FCSTD DOCUMENT  (FreeCAD 1.0R39109 (Git))
Label: asm_cam_mount
License: All rights reserved
LicenseURL: https://en.wikipedia.org/wiki/All_rights_reserved
objects: App::Link×10, App::FeaturePython×10, Assembly::JointGroup×1, Assembly::AssemblyObject×1
EXTERNAL_REF file=../parts/cam_holder/cam_holder_base.FCStd obj=Body
EXTERNAL_REF file=../downloads/raspberry_pi_camera.FCStd obj=Raspberry_Pi_HQ_Camera_with_cs_mount_lens_v3
EXTERNAL_REF file=../secondary/bolts.FCStd obj=Body003
EXTERNAL_REF file=../secondary/bolts.FCStd obj=Body002

FEATURE [App::Link] cam_holder_base
  LinkPlacement = pos=(0,0,0) rot=(1,0,0;3.14159rad)
  LinkedObject = -> <external ../parts/cam_holder/cam_holder_base.FCStd>#Body
  Placement = pos=(0,0,0) rot=(1,0,0;3.14159rad)
FEATURE [App::FeaturePython] GroundedJoint  # Assembly grounded joint (typed FeaturePython)
  ObjectToGround = -> cam_holder_base
  Placement = pos=(0,0,0) rot=(1,0,0;3.14159rad)
FEATURE [App::Link] Raspberry_Pi_HQ_Camera_with_cs_mount_lens_v014  label="Raspberry Pi HQ Camera with cs mount lens v014"
  LinkPlacement = pos=(-18.96,19,-3.8) rot=(1,0,0;1.5708rad)
  LinkedObject = -> <external ../downloads/raspberry_pi_camera.FCStd>#Raspberry_Pi_HQ_Camera_with_cs_mount_lens_v3
  Placement = pos=(-18.96,19,-3.8) rot=(1,0,0;1.5708rad)
FEATURE [App::FeaturePython] Joint  label="Fixed"  # Assembly joint (typed FeaturePython)
  Activated = true
  AngleMax = 0
  AngleMin = 0
  Detach1 = false
  Detach2 = false
  Distance = 0
  Distance2 = 0
  EnableAngleMax = false
  EnableAngleMin = false
  EnableLengthMax = false
  EnableLengthMin = false
  JointType = 0 (Fixed)
  LengthMax = 0
  LengthMin = 0
  Placement1 = pos=(-14.96,-15,2.5) rot=(0,0,1;0rad)
  Placement2 = pos=(4,1.3,4) rot=(-1,0,0;1.5708rad)
  Reference1 = -> Assembly [cam_holder_base.Edge44,cam_holder_base.Edge44]
  Reference2 = -> Assembly [Raspberry_Pi_HQ_Camera_with_cs_mount_lens_v014.Part__Feature.Edge16,Raspberry_Pi_HQ_Camera_with_cs_mount_lens_v014.Part__Feature.Edge16]
FEATURE [App::Link] Hex_screw_M2_5_04_0  label="Hex screw M2.5 04.0"
  LinkPlacement = pos=(-7.97317,-20.5575,-6.3) rot=(0,0,1;0rad)
  LinkedObject = -> <external ../secondary/bolts.FCStd>#Body003
  Placement = pos=(-7.97317,-20.5575,-6.3) rot=(0,0,1;0rad)
FEATURE [App::Link] Hex_screw_M2_5_04_001  label="Hex screw M2.5 04.001"
  LinkPlacement = pos=(22.0268,-20.5575,-6.3) rot=(0,0,1;0rad)
  LinkedObject = -> <external ../secondary/bolts.FCStd>#Body003
  Placement = pos=(22.0268,-20.5575,-6.3) rot=(0,0,1;0rad)
FEATURE [App::Link] Hex_screw_M2_5_04_002  label="Hex screw M2.5 04.002"
  LinkPlacement = pos=(22.0268,-50.5575,-6.3) rot=(0,0,1;0rad)
  LinkedObject = -> <external ../secondary/bolts.FCStd>#Body003
  Placement = pos=(22.0268,-50.5575,-6.3) rot=(0,0,1;0rad)
FEATURE [App::Link] Hex_screw_M2_5_04_003  label="Hex screw M2.5 04.003"
  LinkPlacement = pos=(-7.97317,-50.5575,-6.3) rot=(0,0,1;0rad)
  LinkedObject = -> <external ../secondary/bolts.FCStd>#Body003
  Placement = pos=(-7.97317,-50.5575,-6.3) rot=(0,0,1;0rad)
FEATURE [App::FeaturePython] Joint001  label="Fixed001"  # Assembly joint (typed FeaturePython)
  Activated = true
  AngleMax = 0
  AngleMin = 0
  Detach1 = false
  Detach2 = false
  Distance = 0
  Distance2 = 0
  EnableAngleMax = false
  EnableAngleMin = false
  EnableLengthMax = false
  EnableLengthMin = false
  JointType = 0 (Fixed)
  LengthMax = 0
  LengthMin = 0
  Placement1 = pos=(-6.98683,35.5575,2.5) rot=(0,0,1;0rad)
  Placement2 = pos=(4,0,4) rot=(1,0,0;1.5708rad)
  Reference1 = -> Assembly [Hex_screw_M2_5_04_0.Edge4,Hex_screw_M2_5_04_0.Edge4]
  Reference2 = -> Assembly [Raspberry_Pi_HQ_Camera_with_cs_mount_lens_v014.Part__Feature.Edge18,Raspberry_Pi_HQ_Camera_with_cs_mount_lens_v014.Part__Feature.Edge18]
FEATURE [App::FeaturePython] Joint002  label="Fixed002"  # Assembly joint (typed FeaturePython)
  Activated = true
  AngleMax = 0
  AngleMin = 0
  Detach1 = false
  Detach2 = false
  Distance = 0
  Distance2 = 0
  EnableAngleMax = false
  EnableAngleMin = false
  EnableLengthMax = false
  EnableLengthMin = false
  JointType = 0 (Fixed)
  LengthMax = 0
  LengthMin = 0
  Placement1 = pos=(-6.98683,35.5575,2.5) rot=(0,0,1;0rad)
  Placement2 = pos=(34,0,4) rot=(1,0,0;1.5708rad)
  Reference1 = -> Assembly [Hex_screw_M2_5_04_001.Edge4,Hex_screw_M2_5_04_001.Edge4]
  Reference2 = -> Assembly [Raspberry_Pi_HQ_Camera_with_cs_mount_lens_v014.Part__Feature.Edge24,Raspberry_Pi_HQ_Camera_with_cs_mount_lens_v014.Part__Feature.Edge24]
FEATURE [App::FeaturePython] Joint003  label="Fixed003"  # Assembly joint (typed FeaturePython)
  Activated = true
  AngleMax = 0
  AngleMin = 0
  Detach1 = false
  Detach2 = false
  Distance = 0
  Distance2 = 0
  EnableAngleMax = false
  EnableAngleMin = false
  EnableLengthMax = false
  EnableLengthMin = false
  JointType = 0 (Fixed)
  LengthMax = 0
  LengthMin = 0
  Placement1 = pos=(-6.98683,35.5575,2.5) rot=(0,0,1;0rad)
  Placement2 = pos=(34,0,34) rot=(1,0,0;1.5708rad)
  Reference1 = -> Assembly [Hex_screw_M2_5_04_002.Edge4,Hex_screw_M2_5_04_002.Edge4]
  Reference2 = -> Assembly [Raspberry_Pi_HQ_Camera_with_cs_mount_lens_v014.Part__Feature.Edge22,Raspberry_Pi_HQ_Camera_with_cs_mount_lens_v014.Part__Feature.Edge22]
FEATURE [App::FeaturePython] Joint004  label="Fixed004"  # Assembly joint (typed FeaturePython)
  Activated = true
  AngleMax = 0
  AngleMin = 0
  Detach1 = false
  Detach2 = false
  Distance = 0
  Distance2 = 0
  EnableAngleMax = false
  EnableAngleMin = false
  EnableLengthMax = false
  EnableLengthMin = false
  JointType = 0 (Fixed)
  LengthMax = 0
  LengthMin = 0
  Placement1 = pos=(-6.98683,35.5575,2.5) rot=(0,0,1;0rad)
  Placement2 = pos=(4,0,34) rot=(1,0,0;1.5708rad)
  Reference1 = -> Assembly [Hex_screw_M2_5_04_003.Edge4,Hex_screw_M2_5_04_003.Edge4]
  Reference2 = -> Assembly [Raspberry_Pi_HQ_Camera_with_cs_mount_lens_v014.Part__Feature.Edge20,Raspberry_Pi_HQ_Camera_with_cs_mount_lens_v014.Part__Feature.Edge20]
FEATURE [App::Link] Hex_screw_M4_10_0  label="Hex screw M4 10.0"
  LinkPlacement = pos=(-25.9732,-58.0575,-20.5) rot=(0,0,1;0rad)
  LinkedObject = -> <external ../secondary/bolts.FCStd>#Body002
  Placement = pos=(-25.9732,-58.0575,-20.5) rot=(0,0,1;0rad)
FEATURE [App::Link] Hex_screw_M4_10_001  label="Hex screw M4 10.001"
  LinkPlacement = pos=(-25.9732,-20.0575,-20.5) rot=(0,0,1;0rad)
  LinkedObject = -> <external ../secondary/bolts.FCStd>#Body002
  Placement = pos=(-25.9732,-20.0575,-20.5) rot=(0,0,1;0rad)
FEATURE [App::Link] Hex_screw_M4_10_002  label="Hex screw M4 10.002"
  LinkPlacement = pos=(39.9468,-58.0575,-20.5) rot=(0,0,1;0rad)
  LinkedObject = -> <external ../secondary/bolts.FCStd>#Body002
  Placement = pos=(39.9468,-58.0575,-20.5) rot=(0,0,1;0rad)
FEATURE [App::Link] Hex_screw_M4_10_003  label="Hex screw M4 10.003"
  LinkPlacement = pos=(39.9468,-20.0575,-20.5) rot=(0,0,1;0rad)
  LinkedObject = -> <external ../secondary/bolts.FCStd>#Body002
  Placement = pos=(39.9468,-20.0575,-20.5) rot=(0,0,1;0rad)
FEATURE [App::FeaturePython] Joint005  label="Fixed005"  # Assembly joint (typed FeaturePython)
  Activated = true
  AngleMax = 0
  AngleMin = 0
  Detach1 = false
  Detach2 = false
  Distance = 0
  Distance2 = 0
  EnableAngleMax = false
  EnableAngleMin = false
  EnableLengthMax = false
  EnableLengthMin = false
  JointType = 0 (Fixed)
  LengthMax = 0
  LengthMin = 0
  Placement1 = pos=(-6.98683,35.5575,10) rot=(0,0,1;0rad)
  Placement2 = pos=(32.96,-15.5,10.5) rot=(0,0,1;0rad)
  Reference1 = -> Assembly [Hex_screw_M4_10_003.Edge3,Hex_screw_M4_10_003.Edge3]
  Reference2 = -> Assembly [cam_holder_base.Edge93,cam_holder_base.Edge93]
FEATURE [App::FeaturePython] Joint006  label="Fixed006"  # Assembly joint (typed FeaturePython)
  Activated = true
  AngleMax = 0
  AngleMin = 0
  Detach1 = false
  Detach2 = false
  Distance = 0
  Distance2 = 0
  EnableAngleMax = false
  EnableAngleMin = false
  EnableLengthMax = false
  EnableLengthMin = false
  JointType = 0 (Fixed)
  LengthMax = 0
  LengthMin = 0
  Placement1 = pos=(-6.98683,35.5575,10) rot=(0,0,1;0rad)
  Placement2 = pos=(32.96,22.5,10.5) rot=(0,0,1;0rad)
  Reference1 = -> Assembly [Hex_screw_M4_10_002.Edge3,Hex_screw_M4_10_002.Edge3]
  Reference2 = -> Assembly [cam_holder_base.Edge89,cam_holder_base.Edge89]
FEATURE [App::FeaturePython] Joint007  label="Fixed007"  # Assembly joint (typed FeaturePython)
  Activated = true
  AngleMax = 0
  AngleMin = 0
  Detach1 = false
  Detach2 = false
  Distance = 0
  Distance2 = 0
  EnableAngleMax = false
  EnableAngleMin = false
  EnableLengthMax = false
  EnableLengthMin = false
  JointType = 0 (Fixed)
  LengthMax = 0
  LengthMin = 0
  Placement1 = pos=(-6.98683,35.5575,10) rot=(0,0,1;0rad)
  Placement2 = pos=(-32.96,-15.5,10.5) rot=(0,0,1;0rad)
  Reference1 = -> Assembly [Hex_screw_M4_10_001.Edge3,Hex_screw_M4_10_001.Edge3]
  Reference2 = -> Assembly [cam_holder_base.Edge74,cam_holder_base.Edge74]
FEATURE [App::FeaturePython] Joint008  label="Fixed008"  # Assembly joint (typed FeaturePython)
  Activated = true
  AngleMax = 0
  AngleMin = 0
  Detach1 = false
  Detach2 = false
  Distance = 0
  Distance2 = 0
  EnableAngleMax = false
  EnableAngleMin = false
  EnableLengthMax = false
  EnableLengthMin = false
  JointType = 0 (Fixed)
  LengthMax = 0
  LengthMin = 0
  Placement1 = pos=(-6.98683,35.5575,10) rot=(0,0,1;0rad)
  Placement2 = pos=(-32.96,22.5,10.5) rot=(0,0,1;0rad)
  Reference1 = -> Assembly [Hex_screw_M4_10_0.Edge3,Hex_screw_M4_10_0.Edge3]
  Reference2 = -> Assembly [cam_holder_base.Edge85,cam_holder_base.Edge85]
FEATURE [Assembly::JointGroup] Joints
  Group = -> [GroundedJoint,Joint,Joint001,Joint002,Joint003,Joint004,Joint005,Joint006,Joint007,Joint008]
FEATURE [Assembly::AssemblyObject] Assembly  label="asm_cam_mount"
  Group = -> [Joints,cam_holder_base,GroundedJoint,Raspberry_Pi_HQ_Camera_with_cs_mount_lens_v014,Joint,Hex_screw_M2_5_04_0,Hex_screw_M2_5_04_001,Hex_screw_M2_5_04_002,Hex_screw_M2_5_04_003,Joint001,Joint002,Joint003,Joint004,Hex_screw_M4_10_0,Hex_screw_M4_10_001,Hex_screw_M4_10_002,Hex_screw_M4_10_003,Joint005,Joint006,Joint007,Joint008]
  Origin = -> Origin
  Type = Assembly

RESOLVED EXTERNAL PARTS (link-assembly join: the EXTERNAL_REF files above that resolve inside this repo's crawl, each included once):
---- part ../parts/cam_holder/cam_holder_base.FCStd = doc fcstd_f22dad3d8907 ----
FCSTD DOCUMENT  (FreeCAD 1.0R39109 (Git))
Label: cam_holder_base
License: All rights reserved
LicenseURL: https://en.wikipedia.org/wiki/All_rights_reserved
objects: Sketcher::SketchObject×4, PartDesign::Pad×3, PartDesign::Body×1
note: 18 computed .brp shape members not serialized (recipe doc carries the construction recipe); baked Part::Feature solids carry a one-line shape summary decoded from their .brp

FEATURE [Sketcher::SketchObject] Sketch
  ArcFitTolerance = 0
  FullyConstrained = true
  MakeInternals = false
  sketch-geometry (27):
    g0: LineSegment [constr] StartX=-19.96 StartY=19 StartZ=0 EndX=-19.96 EndY=-14 EndZ=0
    g1: LineSegment StartX=-19.96 StartY=-19 StartZ=0 EndX=-11.96 EndY=-19 EndZ=0
    g2: LineSegment [constr] StartX=20 StartY=-14 StartZ=0 EndX=20 EndY=19 EndZ=0
    g3: LineSegment [constr] StartX=20 StartY=19 StartZ=0 EndX=-19.96 EndY=19 EndZ=0
    g4: GeomPoint [constr] X=0 Y=0 Z=0
    g5: Circle CenterX=-14.96 CenterY=15 CenterZ=0 NormalX=0 NormalY=0 NormalZ=1 AngleXU=0 Radius=1.725
    g6: Circle CenterX=15 CenterY=15 CenterZ=0 NormalX=0 NormalY=0 NormalZ=1 AngleXU=0 Radius=1.725
    g7: Circle CenterX=-14.96 CenterY=-15 CenterZ=0 NormalX=0 NormalY=0 NormalZ=1 AngleXU=0 Radius=1.725
    g8: Circle CenterX=15 CenterY=-15 CenterZ=0 NormalX=0 NormalY=0 NormalZ=1 AngleXU=0 Radius=1.725
    g9: ArcOfCircle CenterX=0 CenterY=0 CenterZ=0 NormalX=0 NormalY=0 NormalZ=1 AngleXU=0 Radius=18.05 StartAngle=5.41371 EndAngle=7.54435
    g10: LineSegment StartX=-11.96 StartY=-19 StartZ=0 EndX=-11.96 EndY=-15 EndZ=0
    g11: LineSegment StartX=11.96 StartY=-19 StartZ=0 EndX=11.96 EndY=-15 EndZ=0
    g12: LineSegment StartX=11.96 StartY=-19 StartZ=0 EndX=20.04 EndY=-19 EndZ=0
    g13: LineSegment StartX=-5.5 StartY=21.5 StartZ=0 EndX=5.5 EndY=21.5 EndZ=0
    g14: LineSegment StartX=-5.5 StartY=21.5 StartZ=0 EndX=-5.5 EndY=17.1916 EndZ=0
    g15: LineSegment StartX=5.5 StartY=21.5 StartZ=0 EndX=5.5 EndY=17.1916 EndZ=0
    g16: ArcOfCircle CenterX=0 CenterY=0 CenterZ=0 NormalX=0 NormalY=0 NormalZ=1 AngleXU=0 Radius=18.05 StartAngle=1.88043 EndAngle=4.01106
    g17: LineSegment StartX=-20 StartY=26 StartZ=0 EndX=20 EndY=26 EndZ=0
    g18: LineSegment StartX=-11.96 StartY=-15 StartZ=0 EndX=-11.6464 EndY=-13.79 EndZ=0
    g19: LineSegment StartX=11.96 StartY=-15 StartZ=0 EndX=11.6464 EndY=-13.79 EndZ=0
    g20: GeomPoint [constr] X=-19.96 Y=-14 Z=0
    g21: LineSegment StartX=-25.96 StartY=26 StartZ=0 EndX=-25.96 EndY=-19 EndZ=0
    g22: LineSegment StartX=-19.96 StartY=-19 StartZ=0 EndX=-25.96 EndY=-19 EndZ=0
    g23: LineSegment StartX=-20 StartY=26 StartZ=0 EndX=-25.96 EndY=26 EndZ=0
    g24: LineSegment StartX=20.04 StartY=-19 StartZ=0 EndX=25.96 EndY=-19 EndZ=0
    g25: LineSegment StartX=25.96 StartY=-19 StartZ=0 EndX=25.96 EndY=26 EndZ=0
    g26: LineSegment StartX=25.96 StartY=26 StartZ=0 EndX=20 EndY=26 EndZ=0
  constraints (77):
    c: Coincident(g2,g3)
    c: Coincident(g3,g0)
    c: Horizontal(g1)
    c: Horizontal(g3)
    c: Vertical(g0)
    c: Vertical(g2)
    c: Coincident(g4,g-1)
    c: DistanceX(g1,g12) = 40
    c: DistanceY(g1,g0) = 38
    c: Distance(g5,g0) = 5
    c: Distance(g5,g3) = 4
    c: Equal(g5,g6)
    c: Equal(g5,g7)
    c: Equal(g5,g8)
    c: Diameter(g5) = 3.45
    c: Vertical(g6,g8)
    c: Horizontal(g7,g8)
    c: Horizontal(g5,g6)
    c: Vertical(g5,g7)
    c: Distance(g4,g2) = 20
    c: Distance(g6,g2) = 5
    c: Distance(g7,g1) = 4
    c: Distance(g4,g1) = 19
    c: Coincident(g9,g4)
    c: Diameter(g9) = 36.1
    c: Vertical(g10)
    c: Distance(g10) = 4
    c: DistanceX(g1,g10) = 8
    c: Symmetric(g11,g10,g-2)
    c: Parallel(g11,g10)
    c: Coincident(g1,g10)
    c: Coincident(g12,g11)
    c: Horizontal(g13)
    c: Distance(g13,g3) = 2.5
    c: Distance(g13,g-2) = 5.5
    c: DistanceX(g13,g13) = 11
    c: Coincident(g14,g13)
    c: Vertical(g14)
    c: Coincident(g15,g13)
    c: Vertical(g15)
    c: Equal(g9,g16)
    c: Coincident(g9,g15)
    c: Coincident(g16,g14)
    c: Coincident(g9,g16)
    c: Horizontal(g17)
    c: Equal(g10,g11)
    c: Coincident(g18,g10)
    c: Coincident(g18,g16)
    c: Coincident(g19,g11)
    c: Coincident(g19,g9)
    c: Distance(g18) = 1.25
    c: Equal(g19,g18)
    c: Distance(g17,g-2) = 20
    c: DistanceX(g17,g17) = 40
    c: Distance(g20,g1) = 5
    c: Coincident(g20,g0)
    c: Equal(g2,g0)
    c: Horizontal(g12)
    c: DistanceX(g5,g4) = 14.96
    c: Vertical(g21)
    c: DistanceX(g1,g4) = 11.96
    c: Coincident(g22,g1)
    c: Horizontal(g22)
    c: Coincident(g21,g22)
    c: DistanceY(g0,g17) = 7
    c: Horizontal(g23)
    c: Coincident(g23,g21)
    c: DistanceX(g21,g0) = 6
    c: Coincident(g23,g17)
    c: Coincident(g24,g12)
    c: Horizontal(g24)
    c: Coincident(g25,g24)
    c: Vertical(g25)
    c: Coincident(g26,g25)
    c: Coincident(g26,g17)
    c: Horizontal(g26)
    c: Equal(g26,g23)
FEATURE [PartDesign::Pad] Pad
  Direction = (0,0,1)
  Length = 2.5
  Length2 = 10
  Profile = -> Sketch
  ReferenceAxis = -> Sketch [N_Axis]
  Suppressed = false
  Type = 0
FEATURE [Sketcher::SketchObject] Sketch001
  ArcFitTolerance = 1e-06
  AttachmentSupport = -> [Pad]
  FullyConstrained = true
  MakeInternals = false
  MapMode = 5
  Placement = pos=(0,0,2.5) rot=(0,0,1;0rad)
FEATURE [Sketcher::SketchObject] Sketch002
  ArcFitTolerance = 1e-06
  AttachmentSupport = -> [Pad]
  ExternalGeometry = -> [Pad]
  FullyConstrained = true
  MakeInternals = false
  MapMode = 5
  Placement = pos=(0,0,2.5) rot=(0,0,1;0rad)
  sketch-geometry (21):
    g0: LineSegment StartX=-25.96 StartY=26 StartZ=0 EndX=-25.96 EndY=19 EndZ=0
    g1: LineSegment StartX=-25.96 StartY=19 StartZ=0 EndX=-22.96 EndY=19 EndZ=0
    g2: LineSegment StartX=-22.96 StartY=19 StartZ=0 EndX=-22.96 EndY=26 EndZ=0
    g3: GeomPoint [constr] X=-24.46 Y=22.5 Z=0
    g4: LineSegment StartX=-25.96 StartY=-12 StartZ=0 EndX=-25.96 EndY=-19 EndZ=0
    g5: LineSegment StartX=-25.96 StartY=-19 StartZ=0 EndX=-22.96 EndY=-19 EndZ=0
    g6: LineSegment StartX=-22.96 StartY=-19 StartZ=0 EndX=-22.96 EndY=-12 EndZ=0
    g7: LineSegment StartX=-22.96 StartY=-12 StartZ=0 EndX=-25.96 EndY=-12 EndZ=0
    g8: GeomPoint [constr] X=-24.46 Y=-15.5 Z=0
    g9: LineSegment StartX=22.96 StartY=-12 StartZ=0 EndX=22.96 EndY=-19 EndZ=0
    g10: LineSegment StartX=22.96 StartY=-19 StartZ=0 EndX=25.96 EndY=-19 EndZ=0
    g11: LineSegment StartX=25.96 StartY=-19 StartZ=0 EndX=25.96 EndY=-12 EndZ=0
    g12: LineSegment StartX=25.96 StartY=-12 StartZ=0 EndX=22.96 EndY=-12 EndZ=0
    g13: GeomPoint [constr] X=24.46 Y=-15.5 Z=0
    g14: GeomPoint X=-22.96 Y=26 Z=0
    g15: LineSegment StartX=-25.96 StartY=26 StartZ=0 EndX=-22.96 EndY=26 EndZ=0
    g16: LineSegment StartX=22.96 StartY=26 StartZ=0 EndX=22.96 EndY=19 EndZ=0
    g17: LineSegment StartX=22.96 StartY=19 StartZ=0 EndX=25.96 EndY=19 EndZ=0
    g18: LineSegment StartX=25.96 StartY=19 StartZ=0 EndX=25.96 EndY=26 EndZ=0
    g19: LineSegment StartX=25.96 StartY=26 StartZ=0 EndX=22.96 EndY=26 EndZ=0
    g20: GeomPoint [constr] X=24.46 Y=22.5 Z=0
  constraints (49):
    c: Coincident(g0,g1)
    c: Coincident(g1,g2)
    c: Vertical(g0)
    c: Vertical(g2)
    c: Horizontal(g1)
    c: Symmetric(g2,g0,g3)
    c: Coincident(g0,g-5)
    c: DistanceY(g0,g0) = 7
    c: Coincident(g4,g5)
    c: Coincident(g5,g6)
    c: Coincident(g6,g7)
    c: Coincident(g7,g4)
    c: Vertical(g4)
    c: Vertical(g6)
    c: Horizontal(g5)
    c: Horizontal(g7)
    c: Symmetric(g6,g4,g8)
    c: Coincident(g9,g10)
    c: Coincident(g10,g11)
    c: Coincident(g11,g12)
    c: Coincident(g12,g9)
    c: Vertical(g9)
    c: Vertical(g11)
    c: Horizontal(g10)
    c: Horizontal(g12)
    c: Symmetric(g11,g9,g13)
    c: Equal(g7,g1)
    c: Equal(g4,g2)
    c: Coincident(g4,g-6)
    c: Equal(g6,g9)
    c: Equal(g7,g12)
    c: Coincident(g10,g-11)
    c: DistanceX(g0,g14) = 3
    c: Coincident(g15,g0)
    c: Coincident(g15,g14)
    c: Horizontal(g15)
    c: Coincident(g2,g14)
    c: Coincident(g16,g17)
    c: Coincident(g17,g18)
    c: Coincident(g18,g19)
    c: Coincident(g19,g16)
    c: Vertical(g16)
    c: Vertical(g18)
    c: Horizontal(g17)
    c: Horizontal(g19)
    c: Symmetric(g18,g16,g20)
    c: Equal(g19,g15)
    c: Equal(g18,g2)
    c: Symmetric(g20,g3,g-2)
FEATURE [PartDesign::Pad] Pad001
  BaseFeature = -> Pad
  Direction = (0,0,1)
  Length = 8
  Length2 = 10
  Profile = -> Sketch002
  ReferenceAxis = -> Sketch002 [N_Axis]
  Refine = true
  Suppressed = false
  Type = 0
FEATURE [Sketcher::SketchObject] Sketch003
  ArcFitTolerance = 1e-06
  AttachmentSupport = -> [Pad001]
  ExternalGeometry = -> [Pad001]
  FullyConstrained = true
  MakeInternals = false
  MapMode = 5
  Placement = pos=(0,0,10.5) rot=(0,0,1;0rad)
  sketch-geometry (20):
    g0: LineSegment StartX=-22.96 StartY=26 StartZ=0 EndX=-22.96 EndY=19 EndZ=0
    g1: LineSegment StartX=-22.96 StartY=19 StartZ=0 EndX=-36.96 EndY=19 EndZ=0
    g2: LineSegment StartX=-36.96 StartY=19 StartZ=0 EndX=-36.96 EndY=26 EndZ=0
    g3: LineSegment StartX=-36.96 StartY=26 StartZ=0 EndX=-22.96 EndY=26 EndZ=0
    g4: LineSegment StartX=-22.96 StartY=-12 StartZ=0 EndX=-36.96 EndY=-12 EndZ=0
    g5: LineSegment StartX=-22.96 StartY=-12 StartZ=0 EndX=-22.96 EndY=-19 EndZ=0
    g6: LineSegment StartX=-22.96 StartY=-19 StartZ=0 EndX=-36.96 EndY=-19 EndZ=0
    g7: LineSegment StartX=-36.96 StartY=-19 StartZ=0 EndX=-36.96 EndY=-12 EndZ=0
    g8: LineSegment StartX=22.96 StartY=-12 StartZ=0 EndX=36.96 EndY=-12 EndZ=0
    g9: LineSegment StartX=22.96 StartY=-12 StartZ=0 EndX=22.96 EndY=-19 EndZ=0
    g10: LineSegment StartX=22.96 StartY=-19 StartZ=0 EndX=36.96 EndY=-19 EndZ=0
    g11: LineSegment StartX=36.96 StartY=-19 StartZ=0 EndX=36.96 EndY=-12 EndZ=0
    g12: Circle CenterX=-32.96 CenterY=22.5 CenterZ=0 NormalX=0 NormalY=0 NormalZ=1 AngleXU=0 Radius=2.1
    g13: Circle CenterX=-32.96 CenterY=-15.5 CenterZ=0 NormalX=0 NormalY=0 NormalZ=1 AngleXU=0 Radius=2.1
    g14: Circle CenterX=32.96 CenterY=22.5 CenterZ=0 NormalX=0 NormalY=0 NormalZ=1 AngleXU=0 Radius=2.1
    g15: Circle CenterX=32.96 CenterY=-15.5 CenterZ=0 NormalX=0 NormalY=0 NormalZ=1 AngleXU=0 Radius=2.1
    g16: LineSegment StartX=22.96 StartY=26 StartZ=0 EndX=36.96 EndY=26 EndZ=0
    g17: LineSegment StartX=36.96 StartY=26 StartZ=0 EndX=36.96 EndY=19 EndZ=0
    g18: LineSegment StartX=36.96 StartY=19 StartZ=0 EndX=22.96 EndY=19 EndZ=0
    g19: LineSegment StartX=22.96 StartY=19 StartZ=0 EndX=22.96 EndY=26 EndZ=0
  constraints (51):
    c: Coincident(g0,g-12)
    c: Coincident(g0,g-12)
    c: Coincident(g1,g0)
    c: Horizontal(g1)
    c: Coincident(g2,g1)
    c: Vertical(g2)
    c: Coincident(g3,g2)
    c: Coincident(g3,g0)
    c: Horizontal(g3)
    c: DistanceX(g1,g1) = 14
    c: Coincident(g4,g-16)
    c: Horizontal(g4)
    c: Coincident(g5,g4)
    c: Coincident(g5,g-15)
    c: Coincident(g6,g5)
    c: Horizontal(g6)
    c: Coincident(g7,g4)
    c: Vertical(g7)
    c: Equal(g6,g1)
    c: Equal(g4,g1)
    c: Equal(g7,g2)
    c: Coincident(g8,g-14)
    c: Horizontal(g8)
    c: Coincident(g9,g8)
    c: Coincident(g9,g-14)
    c: Coincident(g10,g9)
    c: Horizontal(g10)
    c: Coincident(g11,g8)
    c: Vertical(g11)
    c: Diameter(g12) = 4.2
    c: Distance(g12,g2) = 4
    c: Distance(g12,g1) = 3.5
    c: Equal(g13,g12)
    c: Equal(g14,g12)
    c: Symmetric(g12,g14,g-2)
    c: Distance(g13,g7) = 4
    c: Distance(g13,g6) = 3.5
    c: Equal(g14,g15)
    c: Symmetric(g13,g15,g-2)
    c: Coincident(g17,g16)
    c: Vertical(g17)
    c: Horizontal(g18)
    c: Coincident(g19,g16)
    c: Vertical(g19)
    c: Coincident(g18,g19)
    c: Coincident(g17,g18)
    c: Symmetric(g0,g16,g-2)
    c: Symmetric(g2,g16,g-2)
    c: Equal(g0,g19)
    c: Symmetric(g11,g6,g-2)
    c: Equal(g10,g6)
FEATURE [PartDesign::Pad] Pad002
  BaseFeature = -> Pad001
  Direction = (0,0,1)
  Length = 2
  Length2 = 10
  Profile = -> Sketch003
  ReferenceAxis = -> Sketch003 [N_Axis]
  Refine = true
  Suppressed = false
  Type = 0
FEATURE [PartDesign::Body] Body  label="cam_holder_base"
  AllowCompound = false
  Group = -> [Sketch,Pad,Sketch001,Sketch002,Pad001,Sketch003,Pad002]
  Origin = -> Origin
  Tip = -> Pad002
---- part ../secondary/bolts.FCStd = doc fcstd_e978128cc4a6 ----
FCSTD DOCUMENT  (FreeCAD 1.0R39109 (Git))
Label: bolts
License: All rights reserved
LicenseURL: https://en.wikipedia.org/wiki/All_rights_reserved
objects: Sketcher::SketchObject×8, PartDesign::Pad×8, Part::Feature×7, PartDesign::Body×5
note: 52 computed .brp shape members not serialized (recipe doc carries the construction recipe); baked Part::Feature solids carry a one-line shape summary decoded from their .brp

FEATURE [Part::Feature] BOLTS_part  label="Hex socket head cap screw DIN 912 M4 10.0"
  Placement = pos=(0,-31,0) rot=(0,0,1;0rad)
  shape: bbox 7 x 7 x 24 mm, 12 faces (baked)
FEATURE [Part::Feature] BOLTS_part001  label="Hex socket head cap screw DIN 912 M4 15.0"
  Placement = pos=(0,-20,0) rot=(0,0,1;0rad)
  shape: bbox 7 x 7 x 24 mm, 12 faces (baked)
FEATURE [Part::Feature] BOLTS_part002  label="Hex socket head cap screw DIN 912 M4 20.0"
  Placement = pos=(0,-10,0) rot=(0,0,1;0rad)
  shape: bbox 7 x 7 x 24 mm, 12 faces (baked)
FEATURE [Part::Feature] BOLTS_part003  label="Hex socket head cap screw DIN 912 M5 10.0"
  Placement = pos=(0,-1,0) rot=(0,0,1;0rad)
  shape: bbox 8.5 x 8.5 x 27 mm, 12 faces (baked)
FEATURE [Part::Feature] BOLTS_part004  label="Hex socket head cap screw DIN 912 M5 15.0"
  Placement = pos=(0,9,0) rot=(0,0,1;0rad)
  shape: bbox 8.5 x 8.5 x 27 mm, 12 faces (baked)
FEATURE [Part::Feature] BOLTS_part005  label="Hex socket head cap screw DIN 912 M5 20.0"
  Placement = pos=(0,19,0) rot=(0,0,1;0rad)
  shape: bbox 8.5 x 8.5 x 27 mm, 12 faces (baked)
FEATURE [Part::Feature] BOLTS_part006  label="Hex socket head cap screw DIN 912 M2.5 10.0"
  Placement = pos=(0,35,0) rot=(0,0,1;0rad)
  shape: bbox 4.5 x 4.5 x 19.5 mm, 12 faces (baked)
FEATURE [Sketcher::SketchObject] Sketch
  ArcFitTolerance = 1e-06
  AttachmentSupport = -> [XY_Plane001]
  FullyConstrained = false
  MakeInternals = false
  MapMode = 5
  sketch-geometry (1):
    g0: Circle CenterX=-6.98683 CenterY=35.5575 CenterZ=0 NormalX=0 NormalY=0 NormalZ=1 AngleXU=0 Radius=2.25
  constraints (1):
    c: Diameter(g0) = 4.5
FEATURE [PartDesign::Pad] Pad
  Direction = (0,0,1)
  Length = 2.5
  Length2 = 10
  Profile = -> Sketch
  ReferenceAxis = -> Sketch [N_Axis]
  Refine = true
  Suppressed = false
  Type = 0
FEATURE [Sketcher::SketchObject] Sketch001
  ArcFitTolerance = 1e-06
  AttachmentSupport = -> [Pad]
  ExternalGeometry = -> [Pad]
  FullyConstrained = true
  MakeInternals = false
  MapMode = 5
  Placement = pos=(0,0,2.5) rot=(0,0,1;0rad)
  sketch-geometry (1):
    g0: Circle CenterX=-6.98683 CenterY=35.5575 CenterZ=0 NormalX=0 NormalY=0 NormalZ=1 AngleXU=0 Radius=1.25
  constraints (2):
    c: Coincident(g0,g-3)
    c: Diameter(g0) = 2.5
FEATURE [PartDesign::Pad] Pad001
  BaseFeature = -> Pad
  Direction = (0,0,1)
  Length = 8
  Length2 = 10
  Profile = -> Sketch001
  ReferenceAxis = -> Sketch001 [N_Axis]
  Refine = true
  Suppressed = false
  Type = 0
FEATURE [PartDesign::Body] Body001  label="Hex screw M2.5 08.0"
  AllowCompound = false
  Group = -> [Sketch,Pad,Sketch001,Pad001]
  Origin = -> Origin001
  Tip = -> Pad001
FEATURE [Sketcher::SketchObject] Sketch002
  ArcFitTolerance = 1e-06
  AttachmentSupport = -> [XY_Plane002]
  FullyConstrained = false
  MakeInternals = false
  MapMode = 5
  sketch-geometry (1):
    g0: Circle CenterX=-6.98683 CenterY=35.5575 CenterZ=0 NormalX=0 NormalY=0 NormalZ=1 AngleXU=0 Radius=2
  constraints (1):
    c: Diameter(g0) = 4
FEATURE [PartDesign::Pad] Pad002
  Direction = (0,0,1)
  Length = 10
  Length2 = 10
  Profile = -> Sketch002
  ReferenceAxis = -> Sketch002 [N_Axis]
  Refine = true
  Suppressed = false
  Type = 0
FEATURE [Sketcher::SketchObject] Sketch003
  ArcFitTolerance = 1e-06
  AttachmentSupport = -> [Pad002]
  FullyConstrained = false
  MakeInternals = false
  MapMode = 5
  Placement = pos=(0,0,10) rot=(0,0,1;0rad)
  sketch-geometry (1):
    g0: Circle CenterX=-6.98683 CenterY=35.5575 CenterZ=0 NormalX=0 NormalY=0 NormalZ=1 AngleXU=0 Radius=3.5
  constraints (1):
    c: Diameter(g0) = 7
FEATURE [PartDesign::Pad] Pad003
  BaseFeature = -> Pad002
  Direction = (0,0,1)
  Length = 4
  Length2 = 10
  Profile = -> Sketch003
  ReferenceAxis = -> Sketch003 [N_Axis]
  Refine = true
  Suppressed = false
  Type = 0
FEATURE [PartDesign::Body] Body002  label="Hex screw M4 10.0"
  AllowCompound = false
  Group = -> [Sketch002,Pad002,Sketch003,Pad003]
  Origin = -> Origin002
  Tip = -> Pad003
FEATURE [Sketcher::SketchObject] Sketch004
  ArcFitTolerance = 1e-06
  AttachmentSupport = -> [XY_Plane003]
  FullyConstrained = false
  MakeInternals = false
  MapMode = 5
  sketch-geometry (1):
    g0: Circle CenterX=-6.98683 CenterY=35.5575 CenterZ=0 NormalX=0 NormalY=0 NormalZ=1 AngleXU=0 Radius=2.25
  constraints (1):
    c: Diameter(g0) = 4.5
FEATURE [PartDesign::Pad] Pad004
  Direction = (0,0,1)
  Length = 2.5
  Length2 = 10
  Profile = -> Sketch004
  ReferenceAxis = -> Sketch004 [N_Axis]
  Refine = true
  Suppressed = false
  Type = 0
FEATURE [Sketcher::SketchObject] Sketch005
  ArcFitTolerance = 1e-06
  AttachmentSupport = -> [Pad004]
  ExternalGeometry = -> [Pad004]
  FullyConstrained = true
  MakeInternals = false
  MapMode = 5
  Placement = pos=(0,0,2.5) rot=(0,0,1;0rad)
  sketch-geometry (1):
    g0: Circle CenterX=-6.98683 CenterY=35.5575 CenterZ=0 NormalX=0 NormalY=0 NormalZ=1 AngleXU=0 Radius=1.25
  constraints (2):
    c: Coincident(g0,g-3)
    c: Diameter(g0) = 2.5
FEATURE [PartDesign::Pad] Pad005
  BaseFeature = -> Pad004
  Direction = (0,0,1)
  Length = 4
  Length2 = 10
  Profile = -> Sketch005
  ReferenceAxis = -> Sketch005 [N_Axis]
  Refine = true
  Suppressed = false
  Type = 0
FEATURE [PartDesign::Body] Body003  label="Hex screw M2.5 04.0"
  AllowCompound = false
  Group = -> [Sketch004,Pad004,Sketch005,Pad005]
  Origin = -> Origin003
  Tip = -> Pad005
FEATURE [PartDesign::Body] Body  label="Bolts"
  AllowCompound = false
  Origin = -> Origin
FEATURE [Sketcher::SketchObject] Sketch006
  ArcFitTolerance = 1e-06
  AttachmentSupport = -> [XY_Plane004]
  FullyConstrained = false
  MakeInternals = false
  MapMode = 5
  sketch-geometry (1):
    g0: Circle CenterX=-6.98683 CenterY=35.5575 CenterZ=0 NormalX=0 NormalY=0 NormalZ=1 AngleXU=0 Radius=2.5
  constraints (1):
    c: Diameter(g0) = 5
FEATURE [PartDesign::Pad] Pad006
  Direction = (0,0,1)
  Length = 10
  Length2 = 10
  Profile = -> Sketch006
  ReferenceAxis = -> Sketch006 [N_Axis]
  Refine = true
  Suppressed = false
  Type = 0
FEATURE [Sketcher::SketchObject] Sketch007
  ArcFitTolerance = 1e-06
  AttachmentSupport = -> [Pad006]
  FullyConstrained = false
  MakeInternals = false
  MapMode = 5
  Placement = pos=(0,0,10) rot=(0,0,1;0rad)
  sketch-geometry (1):
    g0: Circle CenterX=-6.98683 CenterY=35.5575 CenterZ=0 NormalX=0 NormalY=0 NormalZ=1 AngleXU=0 Radius=4.25
  constraints (1):
    c: Diameter(g0) = 8.5
FEATURE [PartDesign::Pad] Pad007
  BaseFeature = -> Pad006
  Direction = (0,0,1)
  Length = 4
  Length2 = 10
  Profile = -> Sketch007
  ReferenceAxis = -> Sketch007 [N_Axis]
  Refine = true
  Suppressed = false
  Type = 0
FEATURE [PartDesign::Body] Body004  label="Hex screw M5 10.0"
  AllowCompound = false
  Group = -> [Sketch006,Pad006,Sketch007,Pad007]
  Origin = -> Origin004
  Tip = -> Pad007
